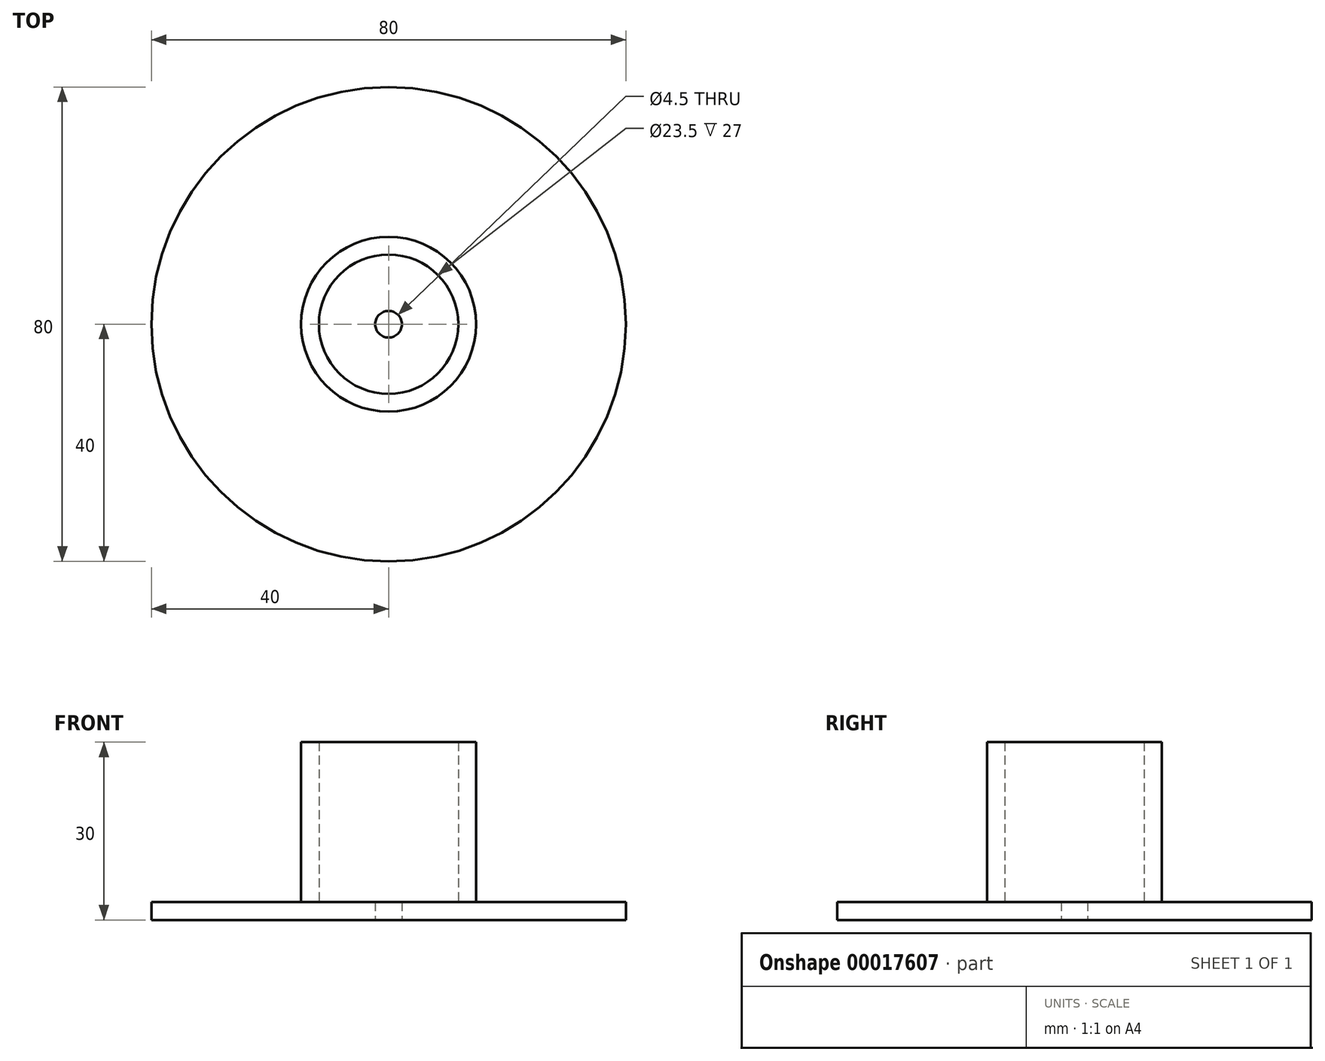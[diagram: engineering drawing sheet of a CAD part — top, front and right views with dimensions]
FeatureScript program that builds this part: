
annotation { "Feature Type Name" : "Feature", "Feature Type Description" : "" }
export const myFeature = defineFeature(function(context is Context, id is Id, definition is map)
    precondition{}
    {
        {
            var Q0;
            Q0=qCreatedBy(makeId("Top.planeOp"),FACE);
            var sketch = newSketch(context, id + "F0", { "sketchPlane" : qUnion([Q0])});
            skCircle(sketch, "E0", {"center": v(0, 0) * mm, "radius": 40 * mm});
            skCircle(sketch, "E1", {"center": v(0, 0) * mm, "radius": 11.75 * mm});
            skCircle(sketch, "E2", {"center": v(0, 0) * mm, "radius": 14.75 * mm});
            skCircle(sketch, "E3", {"center": v(0, 0) * mm, "radius": 2.25 * mm});
            skSolve(sketch);
        }
        {
            var Q0;
            Q0=qSketchRegion(id+"F0",true);
            var Q1;
            Q1=makeQuery(id+"F0.imprint","IMPRINT",FACE,{"disambiguationData":[TD([[makeQuery(id+"F0.imprint","IMPRINT",EDGE,{"derivedFrom":sQuery(id+"F0.wireOp",EDGE,"E1")}),1.0]])]});
            var Q2;
            Q2=makeQuery(id+"F0.imprint","IMPRINT",FACE,{"disambiguationData":[TD([[makeQuery(id+"F0.imprint","IMPRINT",EDGE,{"derivedFrom":sQuery(id+"F0.wireOp",EDGE,"E1")}),-1.0]])]});
            extrude(context, id + "F1", {"entities" : qUnion([Q0, Q1, Q2]), "depth" : 3 * mm});
        }
        {
            var Q0;
            Q0=makeQuery(id+"F0.imprint","IMPRINT",FACE,{"disambiguationData":[TD([[makeQuery(id+"F0.imprint","IMPRINT",EDGE,{"derivedFrom":sQuery(id+"F0.wireOp",EDGE,"E1")}),-1.0]])]});
            extrude(context, id + "F2", {"entities" : qUnion([Q0]), "operationType" : NewBodyOperationType.ADD, "depth" : 30 * mm});
        }
        {
            var Q0;
            Q0=makeQuery(id+"F0.imprint","IMPRINT",FACE,{"disambiguationData":[TD([[makeQuery(id+"F0.imprint","IMPRINT",EDGE,{"derivedFrom":sQuery(id+"F0.wireOp",EDGE,"E0")}),1.0]])]});
            extrude(context, id + "F3", {"entities" : qUnion([Q0]), "operationType" : NewBodyOperationType.ADD, "depth" : 3 * mm});
        }
    });
